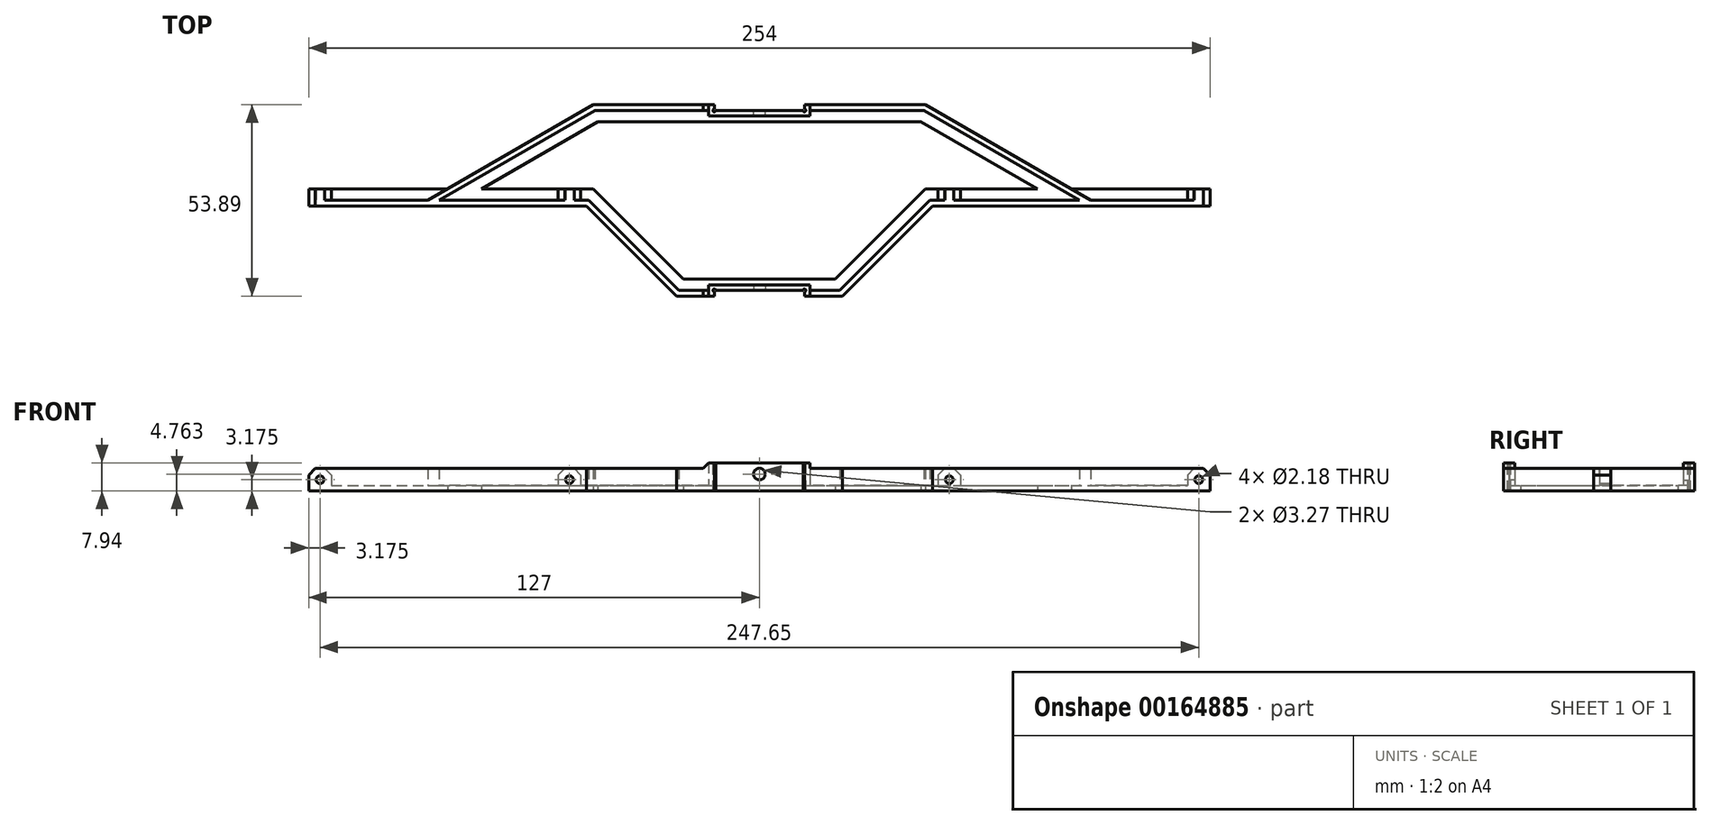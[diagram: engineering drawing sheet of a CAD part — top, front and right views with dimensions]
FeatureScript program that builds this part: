
annotation { "Feature Type Name" : "Feature", "Feature Type Description" : "" }
export const myFeature = defineFeature(function(context is Context, id is Id, definition is map)
    precondition{}
    {
        {
            var Q0;
            Q0=qCreatedBy(makeId("Top.planeOp"),FACE);
            var sketch = newSketch(context, id + "F0", { "sketchPlane" : qUnion([Q0])});
            skLineSegment(sketch, "E0", {"start": v(-127, 25.4) * mm, "end": v(-87.88, 25.4) * mm});
            skLineSegment(sketch, "E1", {"start": v(-46.78, 25.4) * mm, "end": v(-21.38, 0) * mm});
            skLineSegment(sketch, "E2", {"start": v(-21.38, 0) * mm, "end": v(21.38, 0) * mm});
            skLineSegment(sketch, "E3", {"start": v(21.38, 0) * mm, "end": v(46.78, 25.4) * mm});
            skLineSegment(sketch, "E4", {"start": v(87.88, 25.4) * mm, "end": v(127, 25.4) * mm});
            skLineSegment(sketch, "E5", {"start": v(-127, 25.4) * mm, "end": v(-127, 20.64) * mm});
            skLineSegment(sketch, "E6", {"start": v(-127, 20.64) * mm, "end": v(-48.76, 20.64) * mm});
            skLineSegment(sketch, "E7", {"start": v(-48.76, 20.64) * mm, "end": v(-23.36, -4.76) * mm});
            skLineSegment(sketch, "E8", {"start": v(-23.36, -4.76) * mm, "end": v(23.36, -4.76) * mm});
            skLineSegment(sketch, "E9", {"start": v(23.36, -4.76) * mm, "end": v(48.76, 20.64) * mm});
            skLineSegment(sketch, "E10", {"start": v(48.76, 20.64) * mm, "end": v(127, 20.64) * mm});
            skLineSegment(sketch, "E11", {"start": v(127, 20.64) * mm, "end": v(127, 25.4) * mm});
            skLineSegment(sketch, "E12", {"start": v(-34.08, 12.7) * mm, "end": v(-37.45, 9.33) * mm, "construction": true});
            skLineSegment(sketch, "E13", {"start": v(0, 0) * mm, "end": v(0, -4.76) * mm, "construction": true});
            skLineSegment(sketch, "E14", {"start": v(34.08, 12.7) * mm, "end": v(37.45, 9.33) * mm, "construction": true});
            skLineSegment(sketch, "E15", {"start": v(-87.88, 20.64) * mm, "end": v(-87.88, 25.4) * mm, "construction": true});
            skLineSegment(sketch, "E16", {"start": v(87.88, 20.64) * mm, "end": v(87.88, 25.4) * mm, "construction": true});
            skLineSegment(sketch, "E17", {"start": v(-87.88, 25.4) * mm, "end": v(-46.78, 49.13) * mm});
            skLineSegment(sketch, "E18", {"start": v(-78.35, 25.4) * mm, "end": v(-45.5, 44.36) * mm});
            skLineSegment(sketch, "E19", {"start": v(-45.5, 44.36) * mm, "end": v(45.5, 44.36) * mm});
            skLineSegment(sketch, "E20", {"start": v(-46.78, 49.13) * mm, "end": v(46.78, 49.13) * mm});
            skLineSegment(sketch, "E21", {"start": v(-78.35, 25.4) * mm, "end": v(-46.78, 25.4) * mm});
            skLineSegment(sketch, "E22", {"start": v(45.5, 44.36) * mm, "end": v(78.35, 25.4) * mm});
            skLineSegment(sketch, "E23", {"start": v(46.78, 49.13) * mm, "end": v(87.88, 25.4) * mm});
            skLineSegment(sketch, "E24", {"start": v(46.78, 25.4) * mm, "end": v(78.35, 25.4) * mm});
            skLineSegment(sketch, "E25", {"start": v(0, 0) * mm, "end": v(0, 44.36) * mm, "construction": true});
            skLineSegment(sketch, "E26", {"start": v(0, 44.36) * mm, "end": v(0, 49.13) * mm, "construction": true});
            skLineSegment(sketch, "E27", {"start": v(-61.93, 34.88) * mm, "end": v(-64.31, 39) * mm, "construction": true});
            skLineSegment(sketch, "E28", {"start": v(61.93, 34.88) * mm, "end": v(64.31, 39) * mm, "construction": true});
            skLineSegment(sketch, "E29", {"start": v(-46.78, 25.4) * mm, "end": v(0, 25.4) * mm, "construction": true});
            skLineSegment(sketch, "E30", {"start": v(0, 25.4) * mm, "end": v(46.78, 25.4) * mm, "construction": true});
            skSolve(sketch);
        }
        {
            var Q0;
            Q0=qSketchRegion(id+"F0",true);
            extrude(context, id + "F1", {"entities" : qUnion([Q0]), "depth" : 1.59 * mm});
        }
        {
            var Q0;
            Q0=makeQuery(id+"F1.opExtrude","CAP_FACE",FACE,{"disambiguationData":[OSD([sQuery(id+"F0.wireOp",EDGE,"E0"),sQuery(id+"F0.wireOp",EDGE,"E1"),sQuery(id+"F0.wireOp",EDGE,"E2"),sQuery(id+"F0.wireOp",EDGE,"E3"),sQuery(id+"F0.wireOp",EDGE,"E4"),sQuery(id+"F0.wireOp",EDGE,"E5"),sQuery(id+"F0.wireOp",EDGE,"E6"),sQuery(id+"F0.wireOp",EDGE,"E7"),sQuery(id+"F0.wireOp",EDGE,"E8"),sQuery(id+"F0.wireOp",EDGE,"E9"),sQuery(id+"F0.wireOp",EDGE,"E10"),sQuery(id+"F0.wireOp",EDGE,"E11")])],"isStart":false});
            var sketch = newSketch(context, id + "F2", { "sketchPlane" : qUnion([Q0])});
            skLineSegment(sketch, "E31.bottom", {"start": v(-127, 20.64) * mm, "end": v(-48.76, 20.64) * mm});
            skLineSegment(sketch, "E31.top", {"start": v(-127, 22.22) * mm, "end": v(-93.38, 22.22) * mm});
            skLineSegment(sketch, "E31.left", {"start": v(-127, 20.64) * mm, "end": v(-127, 22.22) * mm});
            skLineSegment(sketch, "E32", {"start": v(-48.76, 20.64) * mm, "end": v(-23.36, -4.76) * mm});
            skLineSegment(sketch, "E33", {"start": v(-23.36, -4.76) * mm, "end": v(23.36, -4.76) * mm});
            skLineSegment(sketch, "E34", {"start": v(23.36, -4.76) * mm, "end": v(48.76, 20.64) * mm});
            skLineSegment(sketch, "E35", {"start": v(48.76, 20.64) * mm, "end": v(127, 20.64) * mm});
            skLineSegment(sketch, "E36", {"start": v(127, 20.64) * mm, "end": v(127, 22.22) * mm});
            skLineSegment(sketch, "E37", {"start": v(127, 22.22) * mm, "end": v(93.38, 22.22) * mm});
            skLineSegment(sketch, "E38", {"start": v(48.1, 22.22) * mm, "end": v(22.7, -3.17) * mm});
            skLineSegment(sketch, "E39", {"start": v(-22.7, -3.18) * mm, "end": v(-48.1, 22.22) * mm});
            skLineSegment(sketch, "E40", {"start": v(-36.06, 7.94) * mm, "end": v(-34.93, 9.06) * mm, "construction": true});
            skLineSegment(sketch, "E41", {"start": v(36.06, 7.94) * mm, "end": v(34.93, 9.06) * mm, "construction": true});
            skLineSegment(sketch, "E42", {"start": v(0, -3.18) * mm, "end": v(0, -4.76) * mm, "construction": true});
            skLineSegment(sketch, "E43", {"start": v(-22.7, -3.18) * mm, "end": v(-14.29, -3.18) * mm});
            skLineSegment(sketch, "E44", {"start": v(22.7, -3.18) * mm, "end": v(14.29, -3.18) * mm});
            skLineSegment(sketch, "E45.bottom", {"start": v(-14.29, -3.18) * mm, "end": v(14.29, -3.18) * mm, "construction": true});
            skLineSegment(sketch, "E45.top", {"start": v(-14.29, -1.59) * mm, "end": v(14.29, -1.59) * mm});
            skLineSegment(sketch, "E45.left", {"start": v(-14.29, -3.18) * mm, "end": v(-14.29, -1.59) * mm});
            skLineSegment(sketch, "E45.right", {"start": v(14.29, -3.17) * mm, "end": v(14.29, -1.59) * mm});
            skLineSegment(sketch, "E46", {"start": v(-46.78, 49.13) * mm, "end": v(-93.38, 22.22) * mm});
            skLineSegment(sketch, "E47", {"start": v(-46.78, 49.13) * mm, "end": v(46.78, 49.13) * mm});
            skLineSegment(sketch, "E48", {"start": v(46.78, 49.13) * mm, "end": v(93.38, 22.22) * mm});
            skLineSegment(sketch, "E49", {"start": v(-67.33, 37.26) * mm, "end": v(-66.54, 35.89) * mm, "construction": true});
            skLineSegment(sketch, "E50", {"start": v(0, 49.13) * mm, "end": v(0, 47.54) * mm, "construction": true});
            skLineSegment(sketch, "E51", {"start": v(67.33, 37.26) * mm, "end": v(66.54, 35.89) * mm, "construction": true});
            skLineSegment(sketch, "E52", {"start": v(-90.2, 22.22) * mm, "end": v(-46.36, 47.54) * mm});
            skLineSegment(sketch, "E53", {"start": v(46.36, 47.54) * mm, "end": v(90.2, 22.23) * mm});
            skLineSegment(sketch, "E54", {"start": v(-48.1, 22.22) * mm, "end": v(-90.2, 22.22) * mm});
            skLineSegment(sketch, "E55", {"start": v(48.1, 22.22) * mm, "end": v(90.2, 22.22) * mm});
            skLineSegment(sketch, "E56.bottom", {"start": v(-14.29, 47.54) * mm, "end": v(14.29, 47.54) * mm, "construction": true});
            skLineSegment(sketch, "E56.top", {"start": v(-14.29, 45.95) * mm, "end": v(14.29, 45.95) * mm});
            skLineSegment(sketch, "E56.left", {"start": v(-14.29, 47.54) * mm, "end": v(-14.29, 45.95) * mm});
            skLineSegment(sketch, "E56.right", {"start": v(14.29, 47.54) * mm, "end": v(14.29, 45.95) * mm});
            skLineSegment(sketch, "E57", {"start": v(-14.29, 47.54) * mm, "end": v(-46.36, 47.54) * mm});
            skLineSegment(sketch, "E58", {"start": v(14.29, 47.54) * mm, "end": v(46.36, 47.54) * mm});
            skSolve(sketch);
        }
        {
            var Q0;
            Q0=makeQuery(id+"F2.imprint","IMPRINT",FACE,{"disambiguationData":[TD([[makeQuery(id+"F2.imprint","IMPRINT",EDGE,{"derivedFrom":sQuery(id+"F2.wireOp",EDGE,"E31.bottom")}),1.0]])]});
            extrude(context, id + "F3", {"entities" : qUnion([Q0]), "operationType" : NewBodyOperationType.ADD, "depth" : 4.76 * mm});
        }
        {
            var Q0;
            Q0=makeQuery(id+"F3.opExtrude","SWEPT_FACE",FACE,{"disambiguationData":[OSD([sQuery(id+"F2.wireOp",EDGE,"E31.top")])]});
            var sketch = newSketch(context, id + "F4", { "sketchPlane" : qUnion([Q0])});
            skLineSegment(sketch, "E59.bottom", {"start": v(-50.34, 6.35) * mm, "end": v(-56.7, 6.35) * mm});
            skLineSegment(sketch, "E59.top", {"start": v(-50.34, 0) * mm, "end": v(-56.7, 0) * mm});
            skLineSegment(sketch, "E59.left", {"start": v(-50.34, 6.35) * mm, "end": v(-50.34, 0) * mm});
            skLineSegment(sketch, "E59.right", {"start": v(-56.7, 6.35) * mm, "end": v(-56.7, 0) * mm});
            skLineSegment(sketch, "E60", {"start": v(-50.34, 3.18) * mm, "end": v(-48.76, 3.18) * mm, "construction": true});
            skLineSegment(sketch, "E61.bottom", {"start": v(-127, 6.35) * mm, "end": v(-120.65, 6.35) * mm});
            skLineSegment(sketch, "E61.top", {"start": v(-127, 0) * mm, "end": v(-120.65, 0) * mm});
            skLineSegment(sketch, "E61.left", {"start": v(-127, 6.35) * mm, "end": v(-127, 0) * mm});
            skLineSegment(sketch, "E61.right", {"start": v(-120.65, 6.35) * mm, "end": v(-120.65, 0) * mm});
            skLineSegment(sketch, "E62.bottom", {"start": v(127, 6.35) * mm, "end": v(120.65, 6.35) * mm});
            skLineSegment(sketch, "E62.top", {"start": v(127, 0) * mm, "end": v(120.65, 0) * mm});
            skLineSegment(sketch, "E62.left", {"start": v(127, 6.35) * mm, "end": v(127, 0) * mm});
            skLineSegment(sketch, "E62.right", {"start": v(120.65, 6.35) * mm, "end": v(120.65, 0) * mm});
            skLineSegment(sketch, "E63.bottom", {"start": v(50.34, 6.35) * mm, "end": v(56.7, 6.35) * mm});
            skLineSegment(sketch, "E63.top", {"start": v(50.34, 0) * mm, "end": v(56.7, 0) * mm});
            skLineSegment(sketch, "E63.left", {"start": v(50.34, 6.35) * mm, "end": v(50.34, 0) * mm});
            skLineSegment(sketch, "E63.right", {"start": v(56.7, 6.35) * mm, "end": v(56.7, 0) * mm});
            skLineSegment(sketch, "E64", {"start": v(120.65, 3.18) * mm, "end": v(56.7, 3.18) * mm, "construction": true});
            skLineSegment(sketch, "E65", {"start": v(-56.7, 3.18) * mm, "end": v(-120.65, 3.17) * mm, "construction": true});
            skSolve(sketch);
        }
        {
            var Q0;
            Q0=qSketchRegion(id+"F4",true);
            var Q1;
            Q1=makeQuery(id+"F1.opExtrude","SWEPT_FACE",FACE,{"disambiguationData":[OSD([sQuery(id+"F0.wireOp",EDGE,"E0")])]});
            extrude(context, id + "F5", {"entities" : qUnion([Q0]), "operationType" : NewBodyOperationType.ADD, "endBound" : BoundingType.UP_TO_SURFACE, "endBoundEntityFace" : qUnion([Q1]), "depth" : 25.4 * mm});
        }
        {
            var Q0;
            Q0=makeQuery(id+"F5.boolean.opBoolean","MERGE",EDGE,{"derivedFrom":[makeQuery(id+"F3.opExtrude","CAP_EDGE",EDGE,{"disambiguationData":[OSD([sQuery(id+"F2.wireOp",EDGE,"E31.left")])],"isStart":false}),makeQuery(id+"F5.opExtrude","SWEPT_EDGE",EDGE,{"disambiguationData":[OSD([sQuery(id+"F4.wireOp",EDGE,"E62.bottom"),sQuery(id+"F4.wireOp",EDGE,"E62.left")])]})]});
            var Q1;
            Q1=makeQuery(id+"F5.opExtrude","SWEPT_EDGE",EDGE,{"disambiguationData":[OSD([sQuery(id+"F2.wireOp",EDGE,"E31.top"),sQuery(id+"F4.wireOp",EDGE,"E62.bottom"),sQuery(id+"F4.wireOp",EDGE,"E62.right")])]});
            var Q2;
            Q2=makeQuery(id+"F5.opExtrude","SWEPT_EDGE",EDGE,{"disambiguationData":[OSD([sQuery(id+"F2.wireOp",EDGE,"E31.top"),sQuery(id+"F4.wireOp",EDGE,"E63.bottom"),sQuery(id+"F4.wireOp",EDGE,"E63.right")])]});
            var Q3;
            Q3=makeQuery(id+"F5.opExtrude","SWEPT_EDGE",EDGE,{"disambiguationData":[OSD([sQuery(id+"F2.wireOp",EDGE,"E31.top"),sQuery(id+"F4.wireOp",EDGE,"E63.bottom"),sQuery(id+"F4.wireOp",EDGE,"E63.left")])]});
            var Q4;
            Q4=makeQuery(id+"F5.opExtrude","SWEPT_EDGE",EDGE,{"disambiguationData":[OSD([sQuery(id+"F4.wireOp",EDGE,"E59.bottom"),sQuery(id+"F4.wireOp",EDGE,"E59.left")])]});
            var Q5;
            Q5=makeQuery(id+"F5.opExtrude","SWEPT_EDGE",EDGE,{"disambiguationData":[OSD([sQuery(id+"F4.wireOp",EDGE,"E59.bottom"),sQuery(id+"F4.wireOp",EDGE,"E59.right")])]});
            var Q6;
            Q6=makeQuery(id+"F5.opExtrude","SWEPT_EDGE",EDGE,{"disambiguationData":[OSD([sQuery(id+"F4.wireOp",EDGE,"E61.bottom"),sQuery(id+"F4.wireOp",EDGE,"E61.right")])]});
            var Q7;
            Q7=makeQuery(id+"F5.boolean.opBoolean","MERGE",EDGE,{"derivedFrom":[makeQuery(id+"F3.opExtrude","CAP_EDGE",EDGE,{"disambiguationData":[OSD([sQuery(id+"F2.wireOp",EDGE,"E36")])],"isStart":false}),makeQuery(id+"F5.opExtrude","SWEPT_EDGE",EDGE,{"disambiguationData":[OSD([sQuery(id+"F4.wireOp",EDGE,"E61.bottom"),sQuery(id+"F4.wireOp",EDGE,"E61.left")])]})]});
            chamfer(context, id + "F6", {"entities" : qUnion([Q0, Q1, Q2, Q3, Q4, Q5, Q6, Q7]), "width" : 1.86 * mm, "tangentPropagation" : true});
        }
        {
            var Q0;
            Q0=makeQuery(id+"F5.boolean.opBoolean","MERGE",FACE,{"derivedFrom":[makeQuery(id+"F3.opExtrude","CAP_FACE",FACE,{"disambiguationData":[OSD([sQuery(id+"F2.wireOp",EDGE,"E31.bottom"),sQuery(id+"F2.wireOp",EDGE,"E31.top"),sQuery(id+"F2.wireOp",EDGE,"E31.left"),sQuery(id+"F2.wireOp",EDGE,"E32"),sQuery(id+"F2.wireOp",EDGE,"E33"),sQuery(id+"F2.wireOp",EDGE,"E34"),sQuery(id+"F2.wireOp",EDGE,"E35"),sQuery(id+"F2.wireOp",EDGE,"E36"),sQuery(id+"F2.wireOp",EDGE,"E37"),sQuery(id+"F2.wireOp",EDGE,"E38"),sQuery(id+"F2.wireOp",EDGE,"E39"),sQuery(id+"F2.wireOp",EDGE,"E43"),sQuery(id+"F2.wireOp",EDGE,"E44"),sQuery(id+"F2.wireOp",EDGE,"E45.top"),sQuery(id+"F2.wireOp",EDGE,"E45.left"),sQuery(id+"F2.wireOp",EDGE,"E45.right")])],"isStart":false}),makeQuery(id+"F5.opExtrude","SWEPT_FACE",FACE,{"disambiguationData":[OSD([sQuery(id+"F4.wireOp",EDGE,"E59.bottom")])]}),makeQuery(id+"F5.opExtrude","SWEPT_FACE",FACE,{"disambiguationData":[OSD([sQuery(id+"F4.wireOp",EDGE,"E61.bottom")])]}),makeQuery(id+"F5.opExtrude","SWEPT_FACE",FACE,{"disambiguationData":[OSD([sQuery(id+"F4.wireOp",EDGE,"E62.bottom")])]}),makeQuery(id+"F5.opExtrude","SWEPT_FACE",FACE,{"disambiguationData":[OSD([sQuery(id+"F4.wireOp",EDGE,"E63.bottom")])]})]});
            var sketch = newSketch(context, id + "F7", { "sketchPlane" : qUnion([Q0])});
            skLineSegment(sketch, "E66.bottom", {"start": v(-14.29, -1.59) * mm, "end": v(14.29, -1.59) * mm});
            skLineSegment(sketch, "E66.top", {"start": v(-14.29, -4.76) * mm, "end": v(14.29, -4.76) * mm});
            skLineSegment(sketch, "E66.left", {"start": v(-14.29, -1.59) * mm, "end": v(-14.29, -4.76) * mm});
            skLineSegment(sketch, "E66.right", {"start": v(14.29, -1.59) * mm, "end": v(14.29, -4.76) * mm});
            skLineSegment(sketch, "E67.bottom", {"start": v(-14.29, 45.95) * mm, "end": v(14.29, 45.95) * mm});
            skLineSegment(sketch, "E67.top", {"start": v(-14.29, 49.13) * mm, "end": v(14.29, 49.13) * mm});
            skLineSegment(sketch, "E67.left", {"start": v(-14.29, 45.95) * mm, "end": v(-14.29, 49.13) * mm});
            skLineSegment(sketch, "E67.right", {"start": v(14.29, 45.95) * mm, "end": v(14.29, 49.13) * mm});
            skSolve(sketch);
        }
        {
            var Q0;
            Q0=qSketchRegion(id+"F7",true);
            extrude(context, id + "F8", {"entities" : qUnion([Q0]), "operationType" : NewBodyOperationType.ADD, "depth" : 1.59 * mm});
        }
        {
            var Q0;
            Q0=makeQuery(id+"F8.opExtrude","CAP_FACE",FACE,{"disambiguationData":[OSD([sQuery(id+"F7.wireOp",EDGE,"E67.bottom"),sQuery(id+"F7.wireOp",EDGE,"E67.top"),sQuery(id+"F7.wireOp",EDGE,"E67.left"),sQuery(id+"F7.wireOp",EDGE,"E67.right")])],"isStart":false});
            var sketch = newSketch(context, id + "F9", { "sketchPlane" : qUnion([Q0])});
            skLineSegment(sketch, "E68.bottom", {"start": v(-12.7, -4.76) * mm, "end": v(12.7, -4.76) * mm});
            skLineSegment(sketch, "E68.top", {"start": v(-12.7, -3.18) * mm, "end": v(12.7, -3.18) * mm});
            skLineSegment(sketch, "E68.left", {"start": v(-12.7, -4.76) * mm, "end": v(-12.7, -3.18) * mm});
            skLineSegment(sketch, "E68.right", {"start": v(12.7, -4.76) * mm, "end": v(12.7, -3.18) * mm});
            skLineSegment(sketch, "E69.bottom", {"start": v(-12.7, -3.18) * mm, "end": v(-14.29, -3.18) * mm, "construction": true});
            skLineSegment(sketch, "E69.top", {"start": v(-12.7, -1.59) * mm, "end": v(-14.29, -1.59) * mm, "construction": true});
            skLineSegment(sketch, "E69.left", {"start": v(-12.7, -3.18) * mm, "end": v(-12.7, -1.59) * mm, "construction": true});
            skLineSegment(sketch, "E69.right", {"start": v(-14.29, -3.18) * mm, "end": v(-14.29, -1.59) * mm, "construction": true});
            skLineSegment(sketch, "E70.bottom", {"start": v(12.7, -3.18) * mm, "end": v(14.29, -3.18) * mm, "construction": true});
            skLineSegment(sketch, "E70.top", {"start": v(12.7, -1.59) * mm, "end": v(14.29, -1.59) * mm, "construction": true});
            skLineSegment(sketch, "E70.left", {"start": v(12.7, -3.18) * mm, "end": v(12.7, -1.59) * mm, "construction": true});
            skLineSegment(sketch, "E70.right", {"start": v(14.29, -3.18) * mm, "end": v(14.29, -1.59) * mm, "construction": true});
            skLineSegment(sketch, "E71.bottom", {"start": v(-14.29, 45.95) * mm, "end": v(-12.7, 45.95) * mm, "construction": true});
            skLineSegment(sketch, "E71.top", {"start": v(-14.29, 47.54) * mm, "end": v(-12.7, 47.54) * mm, "construction": true});
            skLineSegment(sketch, "E71.left", {"start": v(-14.29, 45.95) * mm, "end": v(-14.29, 47.54) * mm, "construction": true});
            skLineSegment(sketch, "E71.right", {"start": v(-12.7, 45.95) * mm, "end": v(-12.7, 47.54) * mm, "construction": true});
            skLineSegment(sketch, "E72.bottom", {"start": v(14.29, 47.54) * mm, "end": v(12.7, 47.54) * mm, "construction": true});
            skLineSegment(sketch, "E72.top", {"start": v(14.29, 45.95) * mm, "end": v(12.7, 45.95) * mm, "construction": true});
            skLineSegment(sketch, "E72.left", {"start": v(14.29, 47.54) * mm, "end": v(14.29, 45.95) * mm, "construction": true});
            skLineSegment(sketch, "E72.right", {"start": v(12.7, 47.54) * mm, "end": v(12.7, 45.95) * mm, "construction": true});
            skLineSegment(sketch, "E73.bottom", {"start": v(-12.7, 47.54) * mm, "end": v(12.7, 47.54) * mm});
            skLineSegment(sketch, "E73.top", {"start": v(-12.7, 49.13) * mm, "end": v(12.7, 49.13) * mm});
            skLineSegment(sketch, "E73.left", {"start": v(-12.7, 47.54) * mm, "end": v(-12.7, 49.13) * mm});
            skLineSegment(sketch, "E73.right", {"start": v(12.7, 47.54) * mm, "end": v(12.7, 49.13) * mm});
            skSolve(sketch);
        }
        {
            var Q0;
            Q0=qSketchRegion(id+"F9",true);
            var Q1;
            Q1=makeQuery(id+"F1.opExtrude","CAP_FACE",FACE,{"disambiguationData":[OSD([sQuery(id+"F0.wireOp",EDGE,"E0"),sQuery(id+"F0.wireOp",EDGE,"E1"),sQuery(id+"F0.wireOp",EDGE,"E2"),sQuery(id+"F0.wireOp",EDGE,"E3"),sQuery(id+"F0.wireOp",EDGE,"E4"),sQuery(id+"F0.wireOp",EDGE,"E5"),sQuery(id+"F0.wireOp",EDGE,"E6"),sQuery(id+"F0.wireOp",EDGE,"E7"),sQuery(id+"F0.wireOp",EDGE,"E8"),sQuery(id+"F0.wireOp",EDGE,"E9"),sQuery(id+"F0.wireOp",EDGE,"E10"),sQuery(id+"F0.wireOp",EDGE,"E11")])],"isStart":true});
            extrude(context, id + "F10", {"entities" : qUnion([Q0]), "operationType" : NewBodyOperationType.REMOVE, "endBound" : BoundingType.UP_TO_SURFACE, "oppositeDirection" : true, "endBoundEntityFace" : qUnion([Q1]), "depth" : 25.4 * mm});
        }
        {
            var Q0;
            Q0=makeQuery(id+"F10.boolean.opBoolean","COPY",FACE,{"derivedFrom":makeQuery(id+"F10.opExtrude","SWEPT_FACE",FACE,{"disambiguationData":[OSD([sQuery(id+"F9.wireOp",EDGE,"E68.top")])]})});
            var sketch = newSketch(context, id + "F11", { "sketchPlane" : qUnion([Q0])});
            skLineSegment(sketch, "E74", {"start": v(123.82, 6.35) * mm, "end": v(123.82, 0) * mm, "construction": true});
            skLineSegment(sketch, "E75", {"start": v(53.52, 6.35) * mm, "end": v(53.52, 0) * mm, "construction": true});
            skCircle(sketch, "E76", {"center": v(53.52, 3.17) * mm, "radius": 1.1 * mm});
            skCircle(sketch, "E77", {"center": v(123.82, 3.18) * mm, "radius": 1.1 * mm});
            skLineSegment(sketch, "E78", {"start": v(-53.52, 6.35) * mm, "end": v(-53.52, 0) * mm, "construction": true});
            skLineSegment(sketch, "E79", {"start": v(-123.82, 6.35) * mm, "end": v(-123.82, 0) * mm, "construction": true});
            skCircle(sketch, "E80", {"center": v(-123.82, 3.18) * mm, "radius": 1.1 * mm});
            skCircle(sketch, "E81", {"center": v(-53.52, 3.18) * mm, "radius": 1.1 * mm});
            skLineSegment(sketch, "E82", {"start": v(0, 7.94) * mm, "end": v(0, 4.76) * mm, "construction": true});
            skCircle(sketch, "E83", {"center": v(0, 4.76) * mm, "radius": 1.63 * mm});
            skSolve(sketch);
        }
        {
            var Q0;
            Q0=qSketchRegion(id+"F11",true);
            var Q1;
            Q1=makeQuery(id+"F5.boolean.opBoolean","MERGE",FACE,{"derivedFrom":[makeQuery(id+"F1.opExtrude","SWEPT_FACE",FACE,{"disambiguationData":[OSD([sQuery(id+"F0.wireOp",EDGE,"E21")])]}),makeQuery(id+"F5.opExtrude","CAP_FACE",FACE,{"disambiguationData":[OSD([sQuery(id+"F0.wireOp",EDGE,"E0")]),ownerDisambiguation([makeQuery(id+"F5.opExtrude","SWEPT_BODY",BODY,{"disambiguationData":[OSD([sQuery(id+"F4.wireOp",EDGE,"E63.bottom"),sQuery(id+"F4.wireOp",EDGE,"E63.top"),sQuery(id+"F4.wireOp",EDGE,"E63.left"),sQuery(id+"F4.wireOp",EDGE,"E63.right")])]})])],"isStart":false})]});
            extrude(context, id + "F12", {"entities" : qUnion([Q0]), "operationType" : NewBodyOperationType.REMOVE, "endBound" : BoundingType.UP_TO_SURFACE, "oppositeDirection" : true, "endBoundEntityFace" : qUnion([Q1]), "depth" : 25.4 * mm});
        }
        {
            var Q0;
            Q0=makeQuery(id+"F8.opExtrude","CAP_EDGE",EDGE,{"disambiguationData":[OSD([sQuery(id+"F7.wireOp",EDGE,"E66.left")])],"isStart":true});
            var Q1;
            Q1=makeQuery(id+"F8.opExtrude","CAP_EDGE",EDGE,{"disambiguationData":[OSD([sQuery(id+"F7.wireOp",EDGE,"E66.right")])],"isStart":true});
            var Q2;
            Q2=makeQuery(id+"F8.opExtrude","CAP_EDGE",EDGE,{"disambiguationData":[OSD([sQuery(id+"F7.wireOp",EDGE,"E67.left")])],"isStart":true});
            var Q3;
            Q3=makeQuery(id+"F8.opExtrude","CAP_EDGE",EDGE,{"disambiguationData":[OSD([sQuery(id+"F7.wireOp",EDGE,"E67.right")])],"isStart":true});
            chamfer(context, id + "F13", {"entities" : qUnion([Q0, Q1, Q2, Q3]), "width" : 1.59 * mm, "tangentPropagation" : true});
        }
        {
            var Q0;
            Q0=makeQuery(id+"F8.opExtrude","CAP_FACE",FACE,{"disambiguationData":[OSD([sQuery(id+"F7.wireOp",EDGE,"E67.bottom"),sQuery(id+"F7.wireOp",EDGE,"E67.top"),sQuery(id+"F7.wireOp",EDGE,"E67.left"),sQuery(id+"F7.wireOp",EDGE,"E67.right")])],"isStart":false});
            var sketch = newSketch(context, id + "F14", { "sketchPlane" : qUnion([Q0])});
            skCircle(sketch, "E84", {"center": v(-12.7, -3.18) * mm, "radius": 0.4 * mm});
            skCircle(sketch, "E85", {"center": v(12.7, -3.18) * mm, "radius": 0.4 * mm});
            skCircle(sketch, "E86", {"center": v(12.7, 47.54) * mm, "radius": 0.4 * mm});
            skCircle(sketch, "E87", {"center": v(-12.7, 47.54) * mm, "radius": 0.4 * mm});
            skSolve(sketch);
        }
        {
            var Q0;
            Q0=qSketchRegion(id+"F14",true);
            var Q1;
            Q1=makeQuery(id+"F1.opExtrude","CAP_FACE",FACE,{"disambiguationData":[OSD([sQuery(id+"F0.wireOp",EDGE,"E0"),sQuery(id+"F0.wireOp",EDGE,"E1"),sQuery(id+"F0.wireOp",EDGE,"E2"),sQuery(id+"F0.wireOp",EDGE,"E3"),sQuery(id+"F0.wireOp",EDGE,"E4"),sQuery(id+"F0.wireOp",EDGE,"E5"),sQuery(id+"F0.wireOp",EDGE,"E6"),sQuery(id+"F0.wireOp",EDGE,"E7"),sQuery(id+"F0.wireOp",EDGE,"E8"),sQuery(id+"F0.wireOp",EDGE,"E9"),sQuery(id+"F0.wireOp",EDGE,"E10"),sQuery(id+"F0.wireOp",EDGE,"E11")])],"isStart":true});
            extrude(context, id + "F15", {"entities" : qUnion([Q0]), "operationType" : NewBodyOperationType.REMOVE, "endBound" : BoundingType.UP_TO_SURFACE, "oppositeDirection" : true, "endBoundEntityFace" : qUnion([Q1]), "depth" : 25.4 * mm});
        }
        {
            var Q0;
            Q0=makeQuery(id+"F10.boolean.opBoolean","COPY",FACE,{"derivedFrom":makeQuery(id+"F10.opExtrude","SWEPT_FACE",FACE,{"disambiguationData":[OSD([sQuery(id+"F9.wireOp",EDGE,"E73.bottom")])]})});
            var sketch = newSketch(context, id + "F16", { "sketchPlane" : qUnion([Q0])});
            skCircle(sketch, "E88", {"center": v(0, 4.76) * mm, "radius": 1.63 * mm});
            skSolve(sketch);
        }
        {
            var Q0;
            Q0 = qSketchRegion(id + "F16", true);
            var Q1;
            Q1=makeQuery(id+"F8.boolean.opBoolean","MERGE",FACE,{"derivedFrom":[makeQuery(id+"F3.opExtrude","SWEPT_FACE",FACE,{"disambiguationData":[OSD([sQuery(id+"F2.wireOp",EDGE,"E56.top")])]}),makeQuery(id+"F8.opExtrude","SWEPT_FACE",FACE,{"disambiguationData":[OSD([sQuery(id+"F7.wireOp",EDGE,"E67.bottom")])]})]});
            extrude(context, id + "F17", {"entities" : qUnion([Q0]), "operationType" : NewBodyOperationType.REMOVE, "endBound" : BoundingType.UP_TO_SURFACE, "oppositeDirection" : true, "endBoundEntityFace" : qUnion([Q1]), "depth" : 25.4 * mm});
        }
    });
